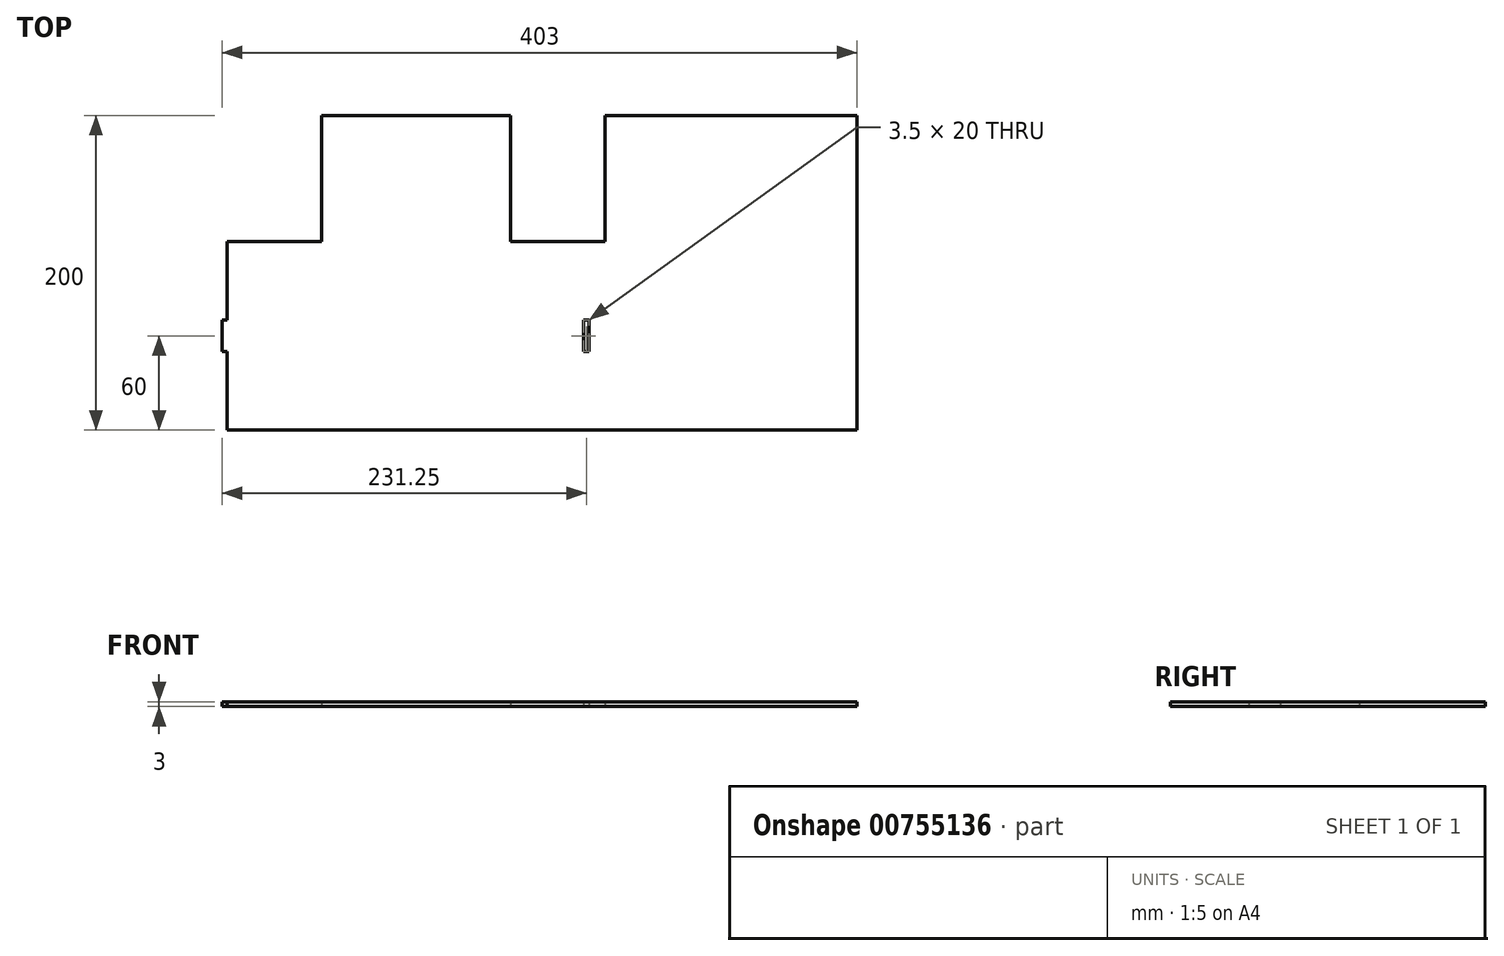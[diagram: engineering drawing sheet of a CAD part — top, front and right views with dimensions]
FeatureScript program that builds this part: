
annotation { "Feature Type Name" : "Feature", "Feature Type Description" : "" }
export const myFeature = defineFeature(function(context is Context, id is Id, definition is map)
    precondition{}
    {
        {
            var Q0;
            Q0=qCreatedBy(makeId("Top.planeOp"),FACE);
            var sketch = newSketch(context, id + "F0", { "sketchPlane" : qUnion([Q0])});
            skLineSegment(sketch, "E0", {"start": v(60, 120) * mm, "end": v(0, 120) * mm});
            skLineSegment(sketch, "E1", {"start": v(0, 120) * mm, "end": v(0, 0) * mm});
            skLineSegment(sketch, "E2", {"start": v(0, 0) * mm, "end": v(400, 0) * mm});
            skLineSegment(sketch, "E3", {"start": v(400, 200) * mm, "end": v(400, 0) * mm});
            skLineSegment(sketch, "E4", {"start": v(240, 200) * mm, "end": v(400, 200) * mm});
            skLineSegment(sketch, "E5", {"start": v(240, 200) * mm, "end": v(240, 120) * mm});
            skLineSegment(sketch, "E6", {"start": v(240, 120) * mm, "end": v(180, 120) * mm});
            skLineSegment(sketch, "E7", {"start": v(180, 200) * mm, "end": v(180, 120) * mm});
            skLineSegment(sketch, "E8", {"start": v(60, 200) * mm, "end": v(180, 200) * mm});
            skLineSegment(sketch, "E9", {"start": v(60, 120) * mm, "end": v(60, 200) * mm});
            skLineSegment(sketch, "E10.bottom", {"start": v(226.5, 70) * mm, "end": v(230, 70) * mm});
            skLineSegment(sketch, "E10.top", {"start": v(226.5, 50) * mm, "end": v(230, 50) * mm});
            skLineSegment(sketch, "E10.left", {"start": v(226.5, 70) * mm, "end": v(226.5, 50) * mm});
            skLineSegment(sketch, "E10.right", {"start": v(230, 70) * mm, "end": v(230, 50) * mm});
            skSolve(sketch);
        }
        {
            var Q0;
            Q0 = qSketchRegion(id + "F0", true);
            extrude(context, id + "F1", {"entities" : qUnion([Q0]), "depth" : 3 * mm, "offsetDistance" : 25 * mm});
        }
        {
            var Q0;
            Q0=makeQuery(id+"F1.opExtrude","CAP_FACE",FACE,{"disambiguationData":[OSD([sQuery(id+"F0.wireOp",EDGE,"E0"),sQuery(id+"F0.wireOp",EDGE,"E1"),sQuery(id+"F0.wireOp",EDGE,"E2"),sQuery(id+"F0.wireOp",EDGE,"E3"),sQuery(id+"F0.wireOp",EDGE,"E4"),sQuery(id+"F0.wireOp",EDGE,"E5"),sQuery(id+"F0.wireOp",EDGE,"E6"),sQuery(id+"F0.wireOp",EDGE,"E7"),sQuery(id+"F0.wireOp",EDGE,"E8"),sQuery(id+"F0.wireOp",EDGE,"E9"),sQuery(id+"F0.wireOp",EDGE,"E10.bottom"),sQuery(id+"F0.wireOp",EDGE,"E10.top"),sQuery(id+"F0.wireOp",EDGE,"E10.left"),sQuery(id+"F0.wireOp",EDGE,"E10.right")])],"isStart":false});
            var sketch = newSketch(context, id + "F2", { "sketchPlane" : qUnion([Q0])});
            skLineSegment(sketch, "E11.bottom", {"start": v(0, 70) * mm, "end": v(-3, 70) * mm});
            skLineSegment(sketch, "E11.top", {"start": v(0, 50) * mm, "end": v(-3, 50) * mm});
            skLineSegment(sketch, "E11.left", {"start": v(0, 70) * mm, "end": v(0, 50) * mm});
            skLineSegment(sketch, "E11.right", {"start": v(-3, 70) * mm, "end": v(-3, 50) * mm});
            skSolve(sketch);
        }
        {
            var Q0;
            Q0 = qSketchRegion(id + "F2", true);
            var Q1;
            Q1=makeQuery(id+"F1.opExtrude","CAP_FACE",FACE,{"disambiguationData":[OSD([sQuery(id+"F0.wireOp",EDGE,"E0"),sQuery(id+"F0.wireOp",EDGE,"E1"),sQuery(id+"F0.wireOp",EDGE,"E2"),sQuery(id+"F0.wireOp",EDGE,"E3"),sQuery(id+"F0.wireOp",EDGE,"E4"),sQuery(id+"F0.wireOp",EDGE,"E5"),sQuery(id+"F0.wireOp",EDGE,"E6"),sQuery(id+"F0.wireOp",EDGE,"E7"),sQuery(id+"F0.wireOp",EDGE,"E8"),sQuery(id+"F0.wireOp",EDGE,"E9"),sQuery(id+"F0.wireOp",EDGE,"E10.bottom"),sQuery(id+"F0.wireOp",EDGE,"E10.top"),sQuery(id+"F0.wireOp",EDGE,"E10.left"),sQuery(id+"F0.wireOp",EDGE,"E10.right")])],"isStart":true});
            extrude(context, id + "F3", {"entities" : qUnion([Q0]), "operationType" : NewBodyOperationType.ADD, "endBound" : BoundingType.UP_TO_SURFACE, "oppositeDirection" : true, "depth" : 25 * mm, "endBoundEntityFace" : qUnion([Q1]), "offsetDistance" : 25 * mm});
        }
    });
